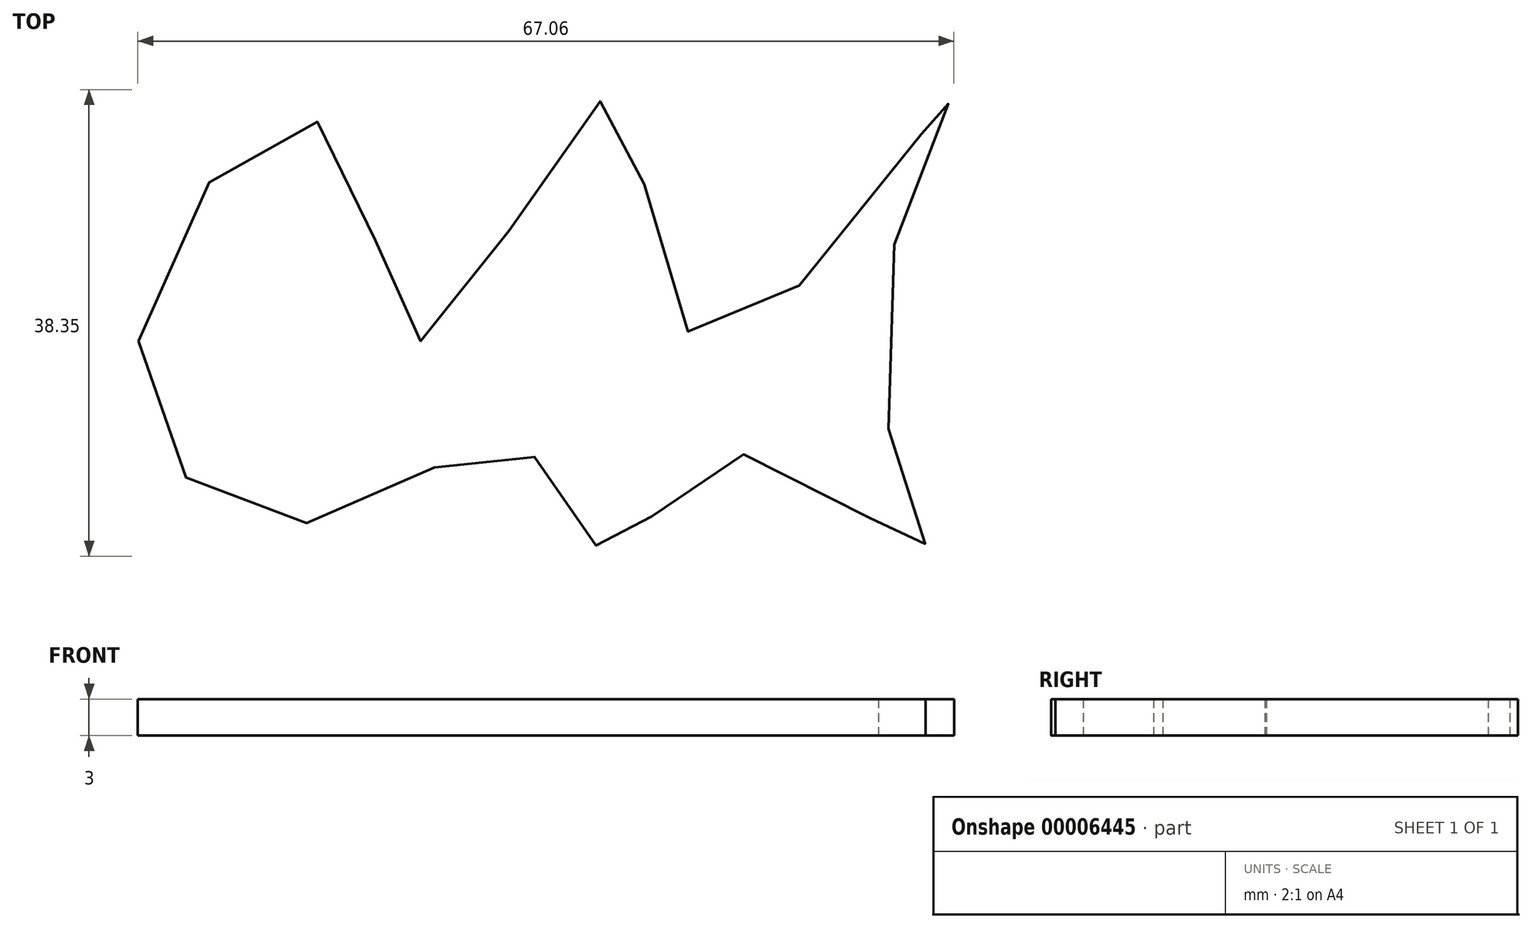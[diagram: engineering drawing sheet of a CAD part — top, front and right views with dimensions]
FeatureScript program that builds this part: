
annotation { "Feature Type Name" : "Feature", "Feature Type Description" : "" }
export const myFeature = defineFeature(function(context is Context, id is Id, definition is map)
    precondition{}
    {
        {
            var Q0;
            Q0=qCreatedBy(makeId("Top.planeOp"),FACE);
            var sketch = newSketch(context, id + "F0", { "sketchPlane" : qUnion([Q0])});
            skFitSpline(sketch, "E0", {"points": [v(-38.9, 0) * mm, v(-23.51, 17.68) * mm, v(-15.73, 0) * mm, v(0, 19.98) * mm, v(7.43, 0) * mm, v(27.93, 20.5) * mm, v(21.92, 0) * mm, v(25.46, -17.33) * mm, v(9.2, -9.37) * mm, v(0, -17.68) * mm, v(-7.43, -8.84) * mm, v(-25.81, -15.03) * mm, v(-38.9, 0) * mm]});
            skSolve(sketch);
        }
        {
            var Q0;
            Q0 = qSketchRegion(id + "F0", true);
            extrude(context, id + "F1", {"entities" : qUnion([Q0]), "depth" : 3 * mm});
        }
    });
